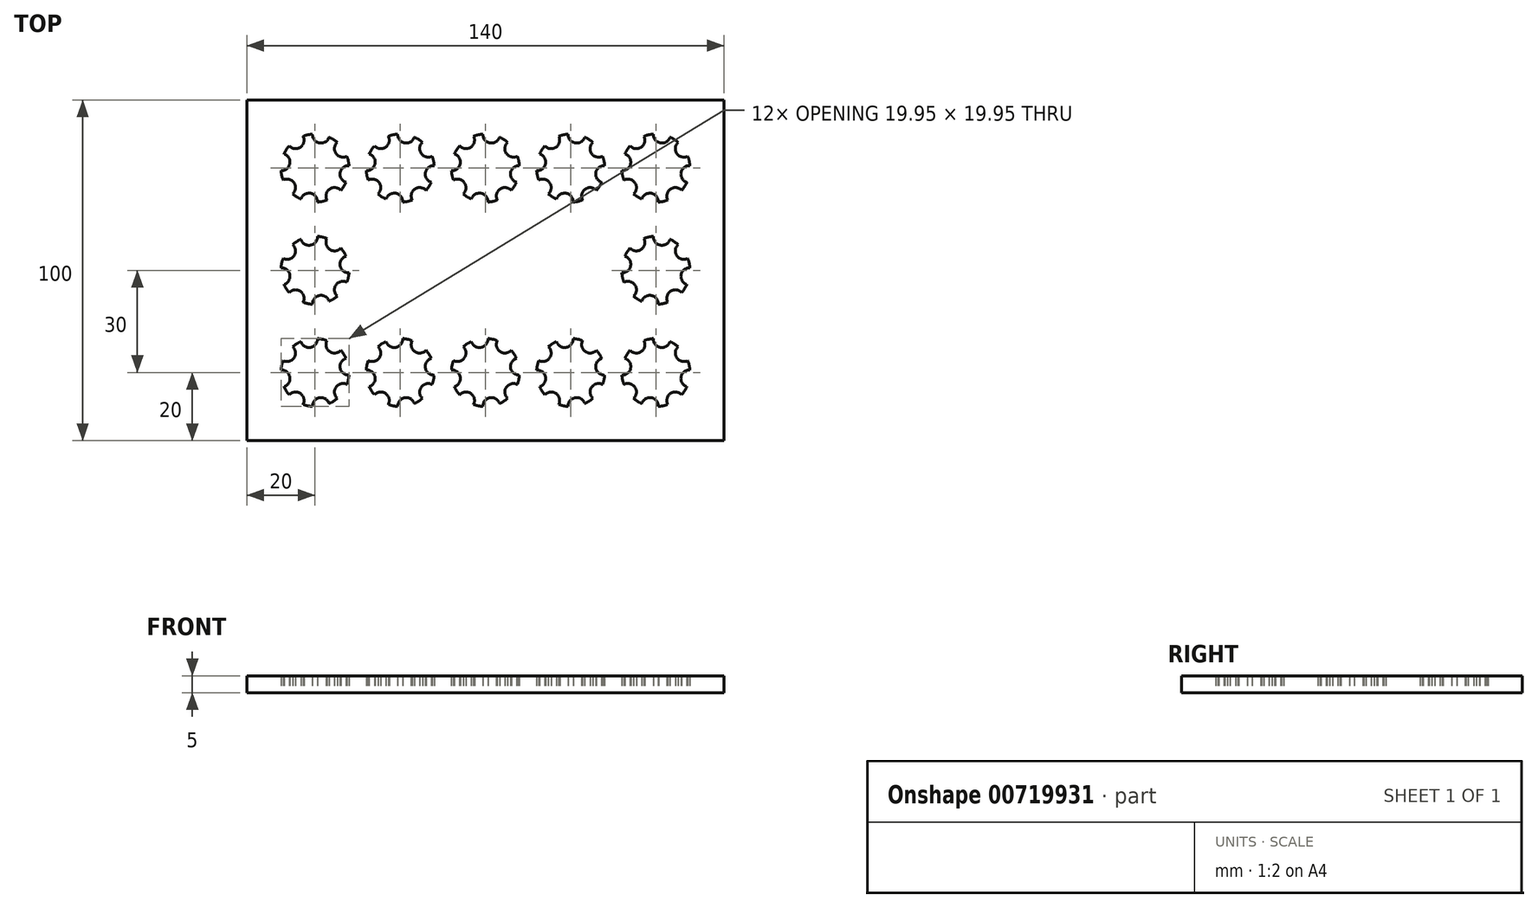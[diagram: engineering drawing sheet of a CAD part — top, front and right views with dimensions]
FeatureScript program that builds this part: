
annotation { "Feature Type Name" : "Feature", "Feature Type Description" : "" }
export const myFeature = defineFeature(function(context is Context, id is Id, definition is map)
    precondition{}
    {
        {
            var Q0;
            Q0=qCreatedBy(makeId("Top.planeOp"),FACE);
            var sketch = newSketch(context, id + "F0", { "sketchPlane" : qUnion([Q0])});
            skLineSegment(sketch, "E0.bottom", {"start": v(0, 100) * mm, "end": v(140, 100) * mm});
            skLineSegment(sketch, "E0.top", {"start": v(0, 0) * mm, "end": v(140, 0) * mm});
            skLineSegment(sketch, "E0.left", {"start": v(0, 100) * mm, "end": v(0, 0) * mm});
            skLineSegment(sketch, "E0.right", {"start": v(140, 100) * mm, "end": v(140, 0) * mm});
            skArc(sketch, "E1", {"start": v(127.57, 73.47) * mm, "mid": v(128.42, 74.6) * mm, "end": v(129.1, 75.85) * mm});
            skArc(sketch, "E2", {"start": v(127.57, 73.47) * mm, "mid": v(124.29, 73.85) * mm, "end": v(123.5, 70.63) * mm});
            skArc(sketch, "E3.1.0", {"start": v(129.97, 80.74) * mm, "mid": v(127.38, 78.68) * mm, "end": v(129.1, 75.85) * mm});
            skArc(sketch, "E3.2.0", {"start": v(126.53, 87.57) * mm, "mid": v(126.15, 84.29) * mm, "end": v(129.37, 83.5) * mm});
            skArc(sketch, "E3.3.0", {"start": v(119.26, 89.97) * mm, "mid": v(121.32, 87.38) * mm, "end": v(124.15, 89.1) * mm});
            skArc(sketch, "E3.4.0", {"start": v(112.43, 86.53) * mm, "mid": v(115.71, 86.15) * mm, "end": v(116.5, 89.37) * mm});
            skArc(sketch, "E3.5.0", {"start": v(110.03, 79.26) * mm, "mid": v(112.62, 81.32) * mm, "end": v(110.9, 84.15) * mm});
            skArc(sketch, "E3.6.0", {"start": v(113.47, 72.43) * mm, "mid": v(113.85, 75.71) * mm, "end": v(110.63, 76.5) * mm});
            skArc(sketch, "E3.7.0", {"start": v(120.74, 70.03) * mm, "mid": v(118.68, 72.62) * mm, "end": v(115.85, 70.9) * mm});
            skArc(sketch, "E4.trimOffspring", {"start": v(129.97, 80.74) * mm, "mid": v(129.77, 82.14) * mm, "end": v(129.37, 83.5) * mm});
            skArc(sketch, "E5.trimOffspring", {"start": v(126.53, 87.57) * mm, "mid": v(125.4, 88.42) * mm, "end": v(124.15, 89.1) * mm});
            skArc(sketch, "E6.trimOffspring", {"start": v(119.26, 89.97) * mm, "mid": v(117.86, 89.77) * mm, "end": v(116.5, 89.37) * mm});
            skArc(sketch, "E7.trimOffspring", {"start": v(112.43, 86.53) * mm, "mid": v(111.58, 85.4) * mm, "end": v(110.9, 84.15) * mm});
            skArc(sketch, "E8.trimOffspring", {"start": v(110.03, 79.26) * mm, "mid": v(110.23, 77.86) * mm, "end": v(110.63, 76.5) * mm});
            skArc(sketch, "E9.trimOffspring", {"start": v(113.47, 72.43) * mm, "mid": v(114.6, 71.58) * mm, "end": v(115.85, 70.9) * mm});
            skArc(sketch, "E10.trimOffspring", {"start": v(120.74, 70.03) * mm, "mid": v(122.14, 70.23) * mm, "end": v(123.5, 70.63) * mm});
            skArc(sketch, "E11.1.0.0", {"start": v(87.43, 86.53) * mm, "mid": v(90.71, 86.15) * mm, "end": v(91.5, 89.37) * mm});
            skArc(sketch, "E11.1.0.1", {"start": v(94.26, 89.97) * mm, "mid": v(92.86, 89.77) * mm, "end": v(91.5, 89.37) * mm});
            skArc(sketch, "E11.1.0.2", {"start": v(94.26, 89.97) * mm, "mid": v(96.32, 87.38) * mm, "end": v(99.15, 89.1) * mm});
            skArc(sketch, "E11.1.0.3", {"start": v(101.53, 87.57) * mm, "mid": v(100.4, 88.42) * mm, "end": v(99.15, 89.1) * mm});
            skArc(sketch, "E11.1.0.4", {"start": v(101.53, 87.57) * mm, "mid": v(101.15, 84.29) * mm, "end": v(104.37, 83.5) * mm});
            skArc(sketch, "E11.1.0.5", {"start": v(104.97, 80.74) * mm, "mid": v(104.77, 82.14) * mm, "end": v(104.37, 83.5) * mm});
            skArc(sketch, "E11.1.0.6", {"start": v(104.97, 80.74) * mm, "mid": v(102.38, 78.68) * mm, "end": v(104.1, 75.85) * mm});
            skArc(sketch, "E11.1.0.7", {"start": v(102.57, 73.47) * mm, "mid": v(103.42, 74.6) * mm, "end": v(104.1, 75.85) * mm});
            skArc(sketch, "E11.1.0.8", {"start": v(102.57, 73.47) * mm, "mid": v(99.29, 73.85) * mm, "end": v(98.5, 70.63) * mm});
            skArc(sketch, "E11.1.0.9", {"start": v(95.74, 70.03) * mm, "mid": v(97.14, 70.23) * mm, "end": v(98.5, 70.63) * mm});
            skArc(sketch, "E11.1.0.10", {"start": v(95.74, 70.03) * mm, "mid": v(93.68, 72.62) * mm, "end": v(90.85, 70.9) * mm});
            skArc(sketch, "E11.1.0.11", {"start": v(88.47, 72.43) * mm, "mid": v(89.6, 71.58) * mm, "end": v(90.85, 70.9) * mm});
            skArc(sketch, "E11.1.0.12", {"start": v(88.47, 72.43) * mm, "mid": v(88.85, 75.71) * mm, "end": v(85.63, 76.5) * mm});
            skArc(sketch, "E11.1.0.13", {"start": v(85.03, 79.26) * mm, "mid": v(85.23, 77.86) * mm, "end": v(85.63, 76.5) * mm});
            skArc(sketch, "E11.1.0.14", {"start": v(85.03, 79.26) * mm, "mid": v(87.62, 81.32) * mm, "end": v(85.9, 84.15) * mm});
            skArc(sketch, "E11.1.0.15", {"start": v(87.43, 86.53) * mm, "mid": v(86.58, 85.4) * mm, "end": v(85.9, 84.15) * mm});
            skArc(sketch, "E11.2.0.0", {"start": v(62.43, 86.53) * mm, "mid": v(65.71, 86.15) * mm, "end": v(66.5, 89.37) * mm});
            skArc(sketch, "E11.2.0.1", {"start": v(69.26, 89.97) * mm, "mid": v(67.86, 89.77) * mm, "end": v(66.5, 89.37) * mm});
            skArc(sketch, "E11.2.0.2", {"start": v(69.26, 89.97) * mm, "mid": v(71.32, 87.38) * mm, "end": v(74.15, 89.1) * mm});
            skArc(sketch, "E11.2.0.3", {"start": v(76.53, 87.57) * mm, "mid": v(75.4, 88.42) * mm, "end": v(74.15, 89.1) * mm});
            skArc(sketch, "E11.2.0.4", {"start": v(76.53, 87.57) * mm, "mid": v(76.15, 84.29) * mm, "end": v(79.37, 83.5) * mm});
            skArc(sketch, "E11.2.0.5", {"start": v(79.97, 80.74) * mm, "mid": v(79.77, 82.14) * mm, "end": v(79.37, 83.5) * mm});
            skArc(sketch, "E11.2.0.6", {"start": v(79.97, 80.74) * mm, "mid": v(77.38, 78.68) * mm, "end": v(79.1, 75.85) * mm});
            skArc(sketch, "E11.2.0.7", {"start": v(77.57, 73.47) * mm, "mid": v(78.42, 74.6) * mm, "end": v(79.1, 75.85) * mm});
            skArc(sketch, "E11.2.0.8", {"start": v(77.57, 73.47) * mm, "mid": v(74.29, 73.85) * mm, "end": v(73.5, 70.63) * mm});
            skArc(sketch, "E11.2.0.9", {"start": v(70.74, 70.03) * mm, "mid": v(72.14, 70.23) * mm, "end": v(73.5, 70.63) * mm});
            skArc(sketch, "E11.2.0.10", {"start": v(70.74, 70.03) * mm, "mid": v(68.68, 72.62) * mm, "end": v(65.85, 70.9) * mm});
            skArc(sketch, "E11.2.0.11", {"start": v(63.47, 72.43) * mm, "mid": v(64.6, 71.58) * mm, "end": v(65.85, 70.9) * mm});
            skArc(sketch, "E11.2.0.12", {"start": v(63.47, 72.43) * mm, "mid": v(63.85, 75.71) * mm, "end": v(60.63, 76.5) * mm});
            skArc(sketch, "E11.2.0.13", {"start": v(60.03, 79.26) * mm, "mid": v(60.23, 77.86) * mm, "end": v(60.63, 76.5) * mm});
            skArc(sketch, "E11.2.0.14", {"start": v(60.03, 79.26) * mm, "mid": v(62.62, 81.32) * mm, "end": v(60.9, 84.15) * mm});
            skArc(sketch, "E11.2.0.15", {"start": v(62.43, 86.53) * mm, "mid": v(61.58, 85.4) * mm, "end": v(60.9, 84.15) * mm});
            skArc(sketch, "E11.3.0.0", {"start": v(37.43, 86.53) * mm, "mid": v(40.71, 86.15) * mm, "end": v(41.5, 89.37) * mm});
            skArc(sketch, "E11.3.0.1", {"start": v(44.26, 89.97) * mm, "mid": v(42.86, 89.77) * mm, "end": v(41.5, 89.37) * mm});
            skArc(sketch, "E11.3.0.2", {"start": v(44.26, 89.97) * mm, "mid": v(46.32, 87.38) * mm, "end": v(49.15, 89.1) * mm});
            skArc(sketch, "E11.3.0.3", {"start": v(51.53, 87.57) * mm, "mid": v(50.4, 88.42) * mm, "end": v(49.15, 89.1) * mm});
            skArc(sketch, "E11.3.0.4", {"start": v(51.53, 87.57) * mm, "mid": v(51.15, 84.29) * mm, "end": v(54.37, 83.5) * mm});
            skArc(sketch, "E11.3.0.5", {"start": v(54.97, 80.74) * mm, "mid": v(54.77, 82.14) * mm, "end": v(54.37, 83.5) * mm});
            skArc(sketch, "E11.3.0.6", {"start": v(54.97, 80.74) * mm, "mid": v(52.38, 78.68) * mm, "end": v(54.1, 75.85) * mm});
            skArc(sketch, "E11.3.0.7", {"start": v(52.57, 73.47) * mm, "mid": v(53.42, 74.6) * mm, "end": v(54.1, 75.85) * mm});
            skArc(sketch, "E11.3.0.8", {"start": v(52.57, 73.47) * mm, "mid": v(49.29, 73.85) * mm, "end": v(48.5, 70.63) * mm});
            skArc(sketch, "E11.3.0.9", {"start": v(45.74, 70.03) * mm, "mid": v(47.14, 70.23) * mm, "end": v(48.5, 70.63) * mm});
            skArc(sketch, "E11.3.0.10", {"start": v(45.74, 70.03) * mm, "mid": v(43.68, 72.62) * mm, "end": v(40.85, 70.9) * mm});
            skArc(sketch, "E11.3.0.11", {"start": v(38.47, 72.43) * mm, "mid": v(39.6, 71.58) * mm, "end": v(40.85, 70.9) * mm});
            skArc(sketch, "E11.3.0.12", {"start": v(38.47, 72.43) * mm, "mid": v(38.85, 75.71) * mm, "end": v(35.63, 76.5) * mm});
            skArc(sketch, "E11.3.0.13", {"start": v(35.03, 79.26) * mm, "mid": v(35.23, 77.86) * mm, "end": v(35.63, 76.5) * mm});
            skArc(sketch, "E11.3.0.14", {"start": v(35.03, 79.26) * mm, "mid": v(37.62, 81.32) * mm, "end": v(35.9, 84.15) * mm});
            skArc(sketch, "E11.3.0.15", {"start": v(37.43, 86.53) * mm, "mid": v(36.58, 85.4) * mm, "end": v(35.9, 84.15) * mm});
            skArc(sketch, "E11.4.0.0", {"start": v(12.43, 86.53) * mm, "mid": v(15.71, 86.15) * mm, "end": v(16.5, 89.37) * mm});
            skArc(sketch, "E11.4.0.1", {"start": v(19.26, 89.97) * mm, "mid": v(17.86, 89.77) * mm, "end": v(16.5, 89.37) * mm});
            skArc(sketch, "E11.4.0.2", {"start": v(19.26, 89.97) * mm, "mid": v(21.32, 87.38) * mm, "end": v(24.15, 89.1) * mm});
            skArc(sketch, "E11.4.0.3", {"start": v(26.53, 87.57) * mm, "mid": v(25.4, 88.42) * mm, "end": v(24.15, 89.1) * mm});
            skArc(sketch, "E11.4.0.4", {"start": v(26.53, 87.57) * mm, "mid": v(26.15, 84.29) * mm, "end": v(29.37, 83.5) * mm});
            skArc(sketch, "E11.4.0.5", {"start": v(29.97, 80.74) * mm, "mid": v(29.77, 82.14) * mm, "end": v(29.37, 83.5) * mm});
            skArc(sketch, "E11.4.0.6", {"start": v(29.97, 80.74) * mm, "mid": v(27.38, 78.68) * mm, "end": v(29.1, 75.85) * mm});
            skArc(sketch, "E11.4.0.7", {"start": v(27.57, 73.47) * mm, "mid": v(28.42, 74.6) * mm, "end": v(29.1, 75.85) * mm});
            skArc(sketch, "E11.4.0.8", {"start": v(27.57, 73.47) * mm, "mid": v(24.29, 73.85) * mm, "end": v(23.5, 70.63) * mm});
            skArc(sketch, "E11.4.0.9", {"start": v(20.74, 70.03) * mm, "mid": v(22.14, 70.23) * mm, "end": v(23.5, 70.63) * mm});
            skArc(sketch, "E11.4.0.10", {"start": v(20.74, 70.03) * mm, "mid": v(18.68, 72.62) * mm, "end": v(15.85, 70.9) * mm});
            skArc(sketch, "E11.4.0.11", {"start": v(13.47, 72.43) * mm, "mid": v(14.6, 71.58) * mm, "end": v(15.85, 70.9) * mm});
            skArc(sketch, "E11.4.0.12", {"start": v(13.47, 72.43) * mm, "mid": v(13.85, 75.71) * mm, "end": v(10.63, 76.5) * mm});
            skArc(sketch, "E11.4.0.13", {"start": v(10.03, 79.26) * mm, "mid": v(10.23, 77.86) * mm, "end": v(10.63, 76.5) * mm});
            skArc(sketch, "E11.4.0.14", {"start": v(10.03, 79.26) * mm, "mid": v(12.62, 81.32) * mm, "end": v(10.9, 84.15) * mm});
            skArc(sketch, "E11.4.0.15", {"start": v(12.43, 86.53) * mm, "mid": v(11.58, 85.4) * mm, "end": v(10.9, 84.15) * mm});
            skLineSegment(sketch, "E11.direction1", {"start": v(112.43, 86.53) * mm, "end": v(87.43, 86.53) * mm, "construction": true});
            skArc(sketch, "E12.0.1.0", {"start": v(127.57, 43.47) * mm, "mid": v(124.29, 43.85) * mm, "end": v(123.5, 40.63) * mm});
            skArc(sketch, "E12.0.1.1", {"start": v(120.74, 40.03) * mm, "mid": v(122.14, 40.23) * mm, "end": v(123.5, 40.63) * mm});
            skArc(sketch, "E12.0.1.2", {"start": v(120.74, 40.03) * mm, "mid": v(118.68, 42.62) * mm, "end": v(115.85, 40.9) * mm});
            skArc(sketch, "E12.0.1.3", {"start": v(113.47, 42.43) * mm, "mid": v(114.6, 41.58) * mm, "end": v(115.85, 40.9) * mm});
            skArc(sketch, "E12.0.1.4", {"start": v(127.57, 43.47) * mm, "mid": v(128.42, 44.6) * mm, "end": v(129.1, 45.85) * mm});
            skArc(sketch, "E12.0.1.5", {"start": v(129.97, 50.74) * mm, "mid": v(127.38, 48.68) * mm, "end": v(129.1, 45.85) * mm});
            skArc(sketch, "E12.0.1.6", {"start": v(129.97, 50.74) * mm, "mid": v(129.77, 52.14) * mm, "end": v(129.37, 53.5) * mm});
            skArc(sketch, "E12.0.1.7", {"start": v(126.53, 57.57) * mm, "mid": v(126.15, 54.29) * mm, "end": v(129.37, 53.5) * mm});
            skArc(sketch, "E12.0.1.8", {"start": v(126.53, 57.57) * mm, "mid": v(125.4, 58.42) * mm, "end": v(124.15, 59.1) * mm});
            skArc(sketch, "E12.0.1.9", {"start": v(119.26, 59.97) * mm, "mid": v(121.32, 57.38) * mm, "end": v(124.15, 59.1) * mm});
            skArc(sketch, "E12.0.1.10", {"start": v(119.26, 59.97) * mm, "mid": v(117.86, 59.77) * mm, "end": v(116.5, 59.37) * mm});
            skArc(sketch, "E12.0.1.11", {"start": v(112.43, 56.53) * mm, "mid": v(115.71, 56.15) * mm, "end": v(116.5, 59.37) * mm});
            skArc(sketch, "E12.0.1.12", {"start": v(112.43, 56.53) * mm, "mid": v(111.58, 55.4) * mm, "end": v(110.9, 54.15) * mm});
            skArc(sketch, "E12.0.1.13", {"start": v(110.03, 49.26) * mm, "mid": v(110.23, 47.86) * mm, "end": v(110.63, 46.5) * mm});
            skArc(sketch, "E12.0.1.14", {"start": v(113.47, 42.43) * mm, "mid": v(113.85, 45.71) * mm, "end": v(110.63, 46.5) * mm});
            skArc(sketch, "E12.0.1.15", {"start": v(110.03, 49.26) * mm, "mid": v(112.62, 51.32) * mm, "end": v(110.9, 54.15) * mm});
            skArc(sketch, "E12.0.2.0", {"start": v(127.57, 13.47) * mm, "mid": v(124.29, 13.85) * mm, "end": v(123.5, 10.63) * mm});
            skArc(sketch, "E12.0.2.1", {"start": v(120.74, 10.03) * mm, "mid": v(122.14, 10.23) * mm, "end": v(123.5, 10.63) * mm});
            skArc(sketch, "E12.0.2.2", {"start": v(120.74, 10.03) * mm, "mid": v(118.68, 12.62) * mm, "end": v(115.85, 10.9) * mm});
            skArc(sketch, "E12.0.2.3", {"start": v(113.47, 12.43) * mm, "mid": v(114.6, 11.58) * mm, "end": v(115.85, 10.9) * mm});
            skArc(sketch, "E12.0.2.4", {"start": v(127.57, 13.47) * mm, "mid": v(128.42, 14.6) * mm, "end": v(129.1, 15.85) * mm});
            skArc(sketch, "E12.0.2.5", {"start": v(129.97, 20.74) * mm, "mid": v(127.38, 18.68) * mm, "end": v(129.1, 15.85) * mm});
            skArc(sketch, "E12.0.2.6", {"start": v(129.97, 20.74) * mm, "mid": v(129.77, 22.14) * mm, "end": v(129.37, 23.5) * mm});
            skArc(sketch, "E12.0.2.7", {"start": v(126.53, 27.57) * mm, "mid": v(126.15, 24.29) * mm, "end": v(129.37, 23.5) * mm});
            skArc(sketch, "E12.0.2.8", {"start": v(126.53, 27.57) * mm, "mid": v(125.4, 28.42) * mm, "end": v(124.15, 29.1) * mm});
            skArc(sketch, "E12.0.2.9", {"start": v(119.26, 29.97) * mm, "mid": v(121.32, 27.38) * mm, "end": v(124.15, 29.1) * mm});
            skArc(sketch, "E12.0.2.10", {"start": v(119.26, 29.97) * mm, "mid": v(117.86, 29.77) * mm, "end": v(116.5, 29.37) * mm});
            skArc(sketch, "E12.0.2.11", {"start": v(112.43, 26.53) * mm, "mid": v(115.71, 26.15) * mm, "end": v(116.5, 29.37) * mm});
            skArc(sketch, "E12.0.2.12", {"start": v(112.43, 26.53) * mm, "mid": v(111.58, 25.4) * mm, "end": v(110.9, 24.15) * mm});
            skArc(sketch, "E12.0.2.13", {"start": v(110.03, 19.26) * mm, "mid": v(110.23, 17.86) * mm, "end": v(110.63, 16.5) * mm});
            skArc(sketch, "E12.0.2.14", {"start": v(113.47, 12.43) * mm, "mid": v(113.85, 15.71) * mm, "end": v(110.63, 16.5) * mm});
            skArc(sketch, "E12.0.2.15", {"start": v(110.03, 19.26) * mm, "mid": v(112.62, 21.32) * mm, "end": v(110.9, 24.15) * mm});
            skLineSegment(sketch, "E12.direction1", {"start": v(123.5, 70.63) * mm, "end": v(148.5, 70.63) * mm, "construction": true});
            skLineSegment(sketch, "E12.direction2", {"start": v(123.5, 70.63) * mm, "end": v(123.5, 40.63) * mm, "construction": true});
            skArc(sketch, "E13.MirrorCS", {"start": v(101.53, 12.43) * mm, "mid": v(101.15, 15.71) * mm, "end": v(104.37, 16.5) * mm});
            skArc(sketch, "E14.MirrorCS", {"start": v(101.53, 12.43) * mm, "mid": v(100.4, 11.58) * mm, "end": v(99.15, 10.9) * mm});
            skArc(sketch, "E15.MirrorCS", {"start": v(104.97, 19.26) * mm, "mid": v(102.38, 21.32) * mm, "end": v(104.1, 24.15) * mm});
            skArc(sketch, "E16.MirrorCS", {"start": v(104.97, 19.26) * mm, "mid": v(104.77, 17.86) * mm, "end": v(104.37, 16.5) * mm});
            skArc(sketch, "E17.MirrorCS", {"start": v(87.43, 13.47) * mm, "mid": v(86.58, 14.6) * mm, "end": v(85.9, 15.85) * mm});
            skArc(sketch, "E18.MirrorCS", {"start": v(10.03, 20.74) * mm, "mid": v(10.23, 22.14) * mm, "end": v(10.63, 23.5) * mm});
            skArc(sketch, "E19.MirrorCS", {"start": v(13.47, 27.57) * mm, "mid": v(13.85, 24.29) * mm, "end": v(10.63, 23.5) * mm});
            skArc(sketch, "E20.MirrorCS", {"start": v(88.47, 27.57) * mm, "mid": v(89.6, 28.42) * mm, "end": v(90.85, 29.1) * mm});
            skArc(sketch, "E21.MirrorCS", {"start": v(87.43, 13.47) * mm, "mid": v(90.71, 13.85) * mm, "end": v(91.5, 10.63) * mm});
            skArc(sketch, "E22.MirrorCS", {"start": v(62.43, 13.47) * mm, "mid": v(65.71, 13.85) * mm, "end": v(66.5, 10.63) * mm});
            skArc(sketch, "E23.MirrorCS", {"start": v(37.43, 13.47) * mm, "mid": v(40.71, 13.85) * mm, "end": v(41.5, 10.63) * mm});
            skArc(sketch, "E24.MirrorCS", {"start": v(79.97, 19.26) * mm, "mid": v(79.77, 17.86) * mm, "end": v(79.37, 16.5) * mm});
            skArc(sketch, "E25.MirrorCS", {"start": v(88.47, 27.57) * mm, "mid": v(88.85, 24.29) * mm, "end": v(85.63, 23.5) * mm});
            skArc(sketch, "E26.MirrorCS", {"start": v(85.03, 20.74) * mm, "mid": v(85.23, 22.14) * mm, "end": v(85.63, 23.5) * mm});
            skArc(sketch, "E27.MirrorCS", {"start": v(38.47, 27.57) * mm, "mid": v(38.85, 24.29) * mm, "end": v(35.63, 23.5) * mm});
            skArc(sketch, "E28.MirrorCS", {"start": v(38.47, 27.57) * mm, "mid": v(39.6, 28.42) * mm, "end": v(40.85, 29.1) * mm});
            skArc(sketch, "E29.MirrorCS", {"start": v(37.43, 13.47) * mm, "mid": v(36.58, 14.6) * mm, "end": v(35.9, 15.85) * mm});
            skArc(sketch, "E30.MirrorCS", {"start": v(44.26, 10.03) * mm, "mid": v(42.86, 10.23) * mm, "end": v(41.5, 10.63) * mm});
            skArc(sketch, "E31.MirrorCS", {"start": v(63.47, 27.57) * mm, "mid": v(63.85, 24.29) * mm, "end": v(60.63, 23.5) * mm});
            skArc(sketch, "E32.MirrorCS", {"start": v(54.97, 19.26) * mm, "mid": v(54.77, 17.86) * mm, "end": v(54.37, 16.5) * mm});
            skArc(sketch, "E33.MirrorCS", {"start": v(51.53, 12.43) * mm, "mid": v(51.15, 15.71) * mm, "end": v(54.37, 16.5) * mm});
            skArc(sketch, "E34.MirrorCS", {"start": v(76.53, 12.43) * mm, "mid": v(76.15, 15.71) * mm, "end": v(79.37, 16.5) * mm});
            skArc(sketch, "E35.MirrorCS", {"start": v(26.53, 12.43) * mm, "mid": v(26.15, 15.71) * mm, "end": v(29.37, 16.5) * mm});
            skArc(sketch, "E36.MirrorCS", {"start": v(45.74, 29.97) * mm, "mid": v(47.14, 29.77) * mm, "end": v(48.5, 29.37) * mm});
            skArc(sketch, "E37.MirrorCS", {"start": v(52.57, 26.53) * mm, "mid": v(49.29, 26.15) * mm, "end": v(48.5, 29.37) * mm});
            skArc(sketch, "E38.MirrorCS", {"start": v(70.74, 29.97) * mm, "mid": v(72.14, 29.77) * mm, "end": v(73.5, 29.37) * mm});
            skArc(sketch, "E39.MirrorCS", {"start": v(51.53, 12.43) * mm, "mid": v(50.4, 11.58) * mm, "end": v(49.15, 10.9) * mm});
            skArc(sketch, "E40.MirrorCS", {"start": v(29.97, 19.26) * mm, "mid": v(29.77, 17.86) * mm, "end": v(29.37, 16.5) * mm});
            skArc(sketch, "E41.MirrorCS", {"start": v(76.53, 12.43) * mm, "mid": v(75.4, 11.58) * mm, "end": v(74.15, 10.9) * mm});
            skArc(sketch, "E42.MirrorCS", {"start": v(27.57, 26.53) * mm, "mid": v(28.42, 25.4) * mm, "end": v(29.1, 24.15) * mm});
            skArc(sketch, "E43.MirrorCS", {"start": v(20.74, 29.97) * mm, "mid": v(22.14, 29.77) * mm, "end": v(23.5, 29.37) * mm});
            skArc(sketch, "E44.MirrorCS", {"start": v(102.57, 26.53) * mm, "mid": v(103.42, 25.4) * mm, "end": v(104.1, 24.15) * mm});
            skArc(sketch, "E45.MirrorCS", {"start": v(77.57, 26.53) * mm, "mid": v(78.42, 25.4) * mm, "end": v(79.1, 24.15) * mm});
            skArc(sketch, "E46.MirrorCS", {"start": v(52.57, 26.53) * mm, "mid": v(53.42, 25.4) * mm, "end": v(54.1, 24.15) * mm});
            skArc(sketch, "E47.MirrorCS", {"start": v(94.26, 10.03) * mm, "mid": v(96.32, 12.62) * mm, "end": v(99.15, 10.9) * mm});
            skArc(sketch, "E48.MirrorCS", {"start": v(19.26, 10.03) * mm, "mid": v(21.32, 12.62) * mm, "end": v(24.15, 10.9) * mm});
            skArc(sketch, "E49.MirrorCS", {"start": v(44.26, 10.03) * mm, "mid": v(46.32, 12.62) * mm, "end": v(49.15, 10.9) * mm});
            skArc(sketch, "E50.MirrorCS", {"start": v(69.26, 10.03) * mm, "mid": v(67.86, 10.23) * mm, "end": v(66.5, 10.63) * mm});
            skArc(sketch, "E51.MirrorCS", {"start": v(29.97, 19.26) * mm, "mid": v(27.38, 21.32) * mm, "end": v(29.1, 24.15) * mm});
            skArc(sketch, "E52.MirrorCS", {"start": v(79.97, 19.26) * mm, "mid": v(77.38, 21.32) * mm, "end": v(79.1, 24.15) * mm});
            skArc(sketch, "E53.MirrorCS", {"start": v(54.97, 19.26) * mm, "mid": v(52.38, 21.32) * mm, "end": v(54.1, 24.15) * mm});
            skArc(sketch, "E54.MirrorCS", {"start": v(102.57, 26.53) * mm, "mid": v(99.29, 26.15) * mm, "end": v(98.5, 29.37) * mm});
            skArc(sketch, "E55.MirrorCS", {"start": v(69.26, 10.03) * mm, "mid": v(71.32, 12.62) * mm, "end": v(74.15, 10.9) * mm});
            skArc(sketch, "E56.MirrorCS", {"start": v(13.47, 27.57) * mm, "mid": v(14.6, 28.42) * mm, "end": v(15.85, 29.1) * mm});
            skArc(sketch, "E57.MirrorCS", {"start": v(70.74, 29.97) * mm, "mid": v(68.68, 27.38) * mm, "end": v(65.85, 29.1) * mm});
            skArc(sketch, "E58.MirrorCS", {"start": v(95.74, 29.97) * mm, "mid": v(93.68, 27.38) * mm, "end": v(90.85, 29.1) * mm});
            skArc(sketch, "E59.MirrorCS", {"start": v(45.74, 29.97) * mm, "mid": v(43.68, 27.38) * mm, "end": v(40.85, 29.1) * mm});
            skArc(sketch, "E60.MirrorCS", {"start": v(62.43, 13.47) * mm, "mid": v(61.58, 14.6) * mm, "end": v(60.9, 15.85) * mm});
            skArc(sketch, "E61.MirrorCS", {"start": v(20.74, 29.97) * mm, "mid": v(18.68, 27.38) * mm, "end": v(15.85, 29.1) * mm});
            skArc(sketch, "E62.MirrorCS", {"start": v(94.26, 10.03) * mm, "mid": v(92.86, 10.23) * mm, "end": v(91.5, 10.63) * mm});
            skArc(sketch, "E63.MirrorCS", {"start": v(19.26, 10.03) * mm, "mid": v(17.86, 10.23) * mm, "end": v(16.5, 10.63) * mm});
            skArc(sketch, "E64.MirrorCS", {"start": v(12.43, 13.47) * mm, "mid": v(15.71, 13.85) * mm, "end": v(16.5, 10.63) * mm});
            skArc(sketch, "E65.MirrorCS", {"start": v(35.03, 20.74) * mm, "mid": v(35.23, 22.14) * mm, "end": v(35.63, 23.5) * mm});
            skArc(sketch, "E66.MirrorCS", {"start": v(63.47, 27.57) * mm, "mid": v(64.6, 28.42) * mm, "end": v(65.85, 29.1) * mm});
            skArc(sketch, "E67.MirrorCS", {"start": v(12.43, 13.47) * mm, "mid": v(11.58, 14.6) * mm, "end": v(10.9, 15.85) * mm});
            skArc(sketch, "E68.MirrorCS", {"start": v(77.57, 26.53) * mm, "mid": v(74.29, 26.15) * mm, "end": v(73.5, 29.37) * mm});
            skArc(sketch, "E69.MirrorCS", {"start": v(26.53, 12.43) * mm, "mid": v(25.4, 11.58) * mm, "end": v(24.15, 10.9) * mm});
            skArc(sketch, "E70.MirrorCS", {"start": v(85.03, 20.74) * mm, "mid": v(87.62, 18.68) * mm, "end": v(85.9, 15.85) * mm});
            skArc(sketch, "E71.MirrorCS", {"start": v(10.03, 20.74) * mm, "mid": v(12.62, 18.68) * mm, "end": v(10.9, 15.85) * mm});
            skArc(sketch, "E72.MirrorCS", {"start": v(27.57, 26.53) * mm, "mid": v(24.29, 26.15) * mm, "end": v(23.5, 29.37) * mm});
            skArc(sketch, "E73.MirrorCS", {"start": v(95.74, 29.97) * mm, "mid": v(97.14, 29.77) * mm, "end": v(98.5, 29.37) * mm});
            skArc(sketch, "E74.MirrorCS", {"start": v(60.03, 20.74) * mm, "mid": v(62.62, 18.68) * mm, "end": v(60.9, 15.85) * mm});
            skArc(sketch, "E75.MirrorCS", {"start": v(35.03, 20.74) * mm, "mid": v(37.62, 18.68) * mm, "end": v(35.9, 15.85) * mm});
            skArc(sketch, "E76.MirrorCS", {"start": v(60.03, 20.74) * mm, "mid": v(60.23, 22.14) * mm, "end": v(60.63, 23.5) * mm});
            skLineSegment(sketch, "E77", {"start": v(70, 100) * mm, "end": v(70, 0) * mm});
            skArc(sketch, "E78.MirrorCS", {"start": v(26.53, 42.43) * mm, "mid": v(25.4, 41.58) * mm, "end": v(24.15, 40.9) * mm});
            skArc(sketch, "E79.MirrorCS", {"start": v(29.97, 49.26) * mm, "mid": v(29.77, 47.86) * mm, "end": v(29.37, 46.5) * mm});
            skArc(sketch, "E80.MirrorCS", {"start": v(26.53, 42.43) * mm, "mid": v(26.15, 45.71) * mm, "end": v(29.37, 46.5) * mm});
            skArc(sketch, "E81.MirrorCS", {"start": v(10.03, 50.74) * mm, "mid": v(12.62, 48.68) * mm, "end": v(10.9, 45.85) * mm});
            skArc(sketch, "E82.MirrorCS", {"start": v(19.26, 40.03) * mm, "mid": v(21.32, 42.62) * mm, "end": v(24.15, 40.9) * mm});
            skArc(sketch, "E83.MirrorCS", {"start": v(27.57, 56.53) * mm, "mid": v(28.42, 55.4) * mm, "end": v(29.1, 54.15) * mm});
            skArc(sketch, "E84.MirrorCS", {"start": v(12.43, 43.47) * mm, "mid": v(11.58, 44.6) * mm, "end": v(10.9, 45.85) * mm});
            skArc(sketch, "E85.MirrorCS", {"start": v(13.47, 57.57) * mm, "mid": v(14.6, 58.42) * mm, "end": v(15.85, 59.1) * mm});
            skArc(sketch, "E86.MirrorCS", {"start": v(19.26, 40.03) * mm, "mid": v(17.86, 40.23) * mm, "end": v(16.5, 40.63) * mm});
            skArc(sketch, "E87.MirrorCS", {"start": v(12.43, 43.47) * mm, "mid": v(15.71, 43.85) * mm, "end": v(16.5, 40.63) * mm});
            skArc(sketch, "E88.MirrorCS", {"start": v(27.57, 56.53) * mm, "mid": v(24.29, 56.15) * mm, "end": v(23.5, 59.37) * mm});
            skArc(sketch, "E89.MirrorCS", {"start": v(13.47, 57.57) * mm, "mid": v(13.85, 54.29) * mm, "end": v(10.63, 53.5) * mm});
            skArc(sketch, "E90.MirrorCS", {"start": v(20.74, 59.97) * mm, "mid": v(22.14, 59.77) * mm, "end": v(23.5, 59.37) * mm});
            skArc(sketch, "E91.MirrorCS", {"start": v(20.74, 59.97) * mm, "mid": v(18.68, 57.38) * mm, "end": v(15.85, 59.1) * mm});
            skArc(sketch, "E92.MirrorCS", {"start": v(29.97, 49.26) * mm, "mid": v(27.38, 51.32) * mm, "end": v(29.1, 54.15) * mm});
            skArc(sketch, "E93.MirrorCS", {"start": v(10.03, 50.74) * mm, "mid": v(10.23, 52.14) * mm, "end": v(10.63, 53.5) * mm});
            skSolve(sketch);
        }
        {
            var Q0;
            Q0 = qSketchRegion(id + "F0", true);
            extrude(context, id + "F1", {"entities" : qUnion([Q0]), "depth" : 5 * mm, "offsetDistance" : 25 * mm});
        }
    });
